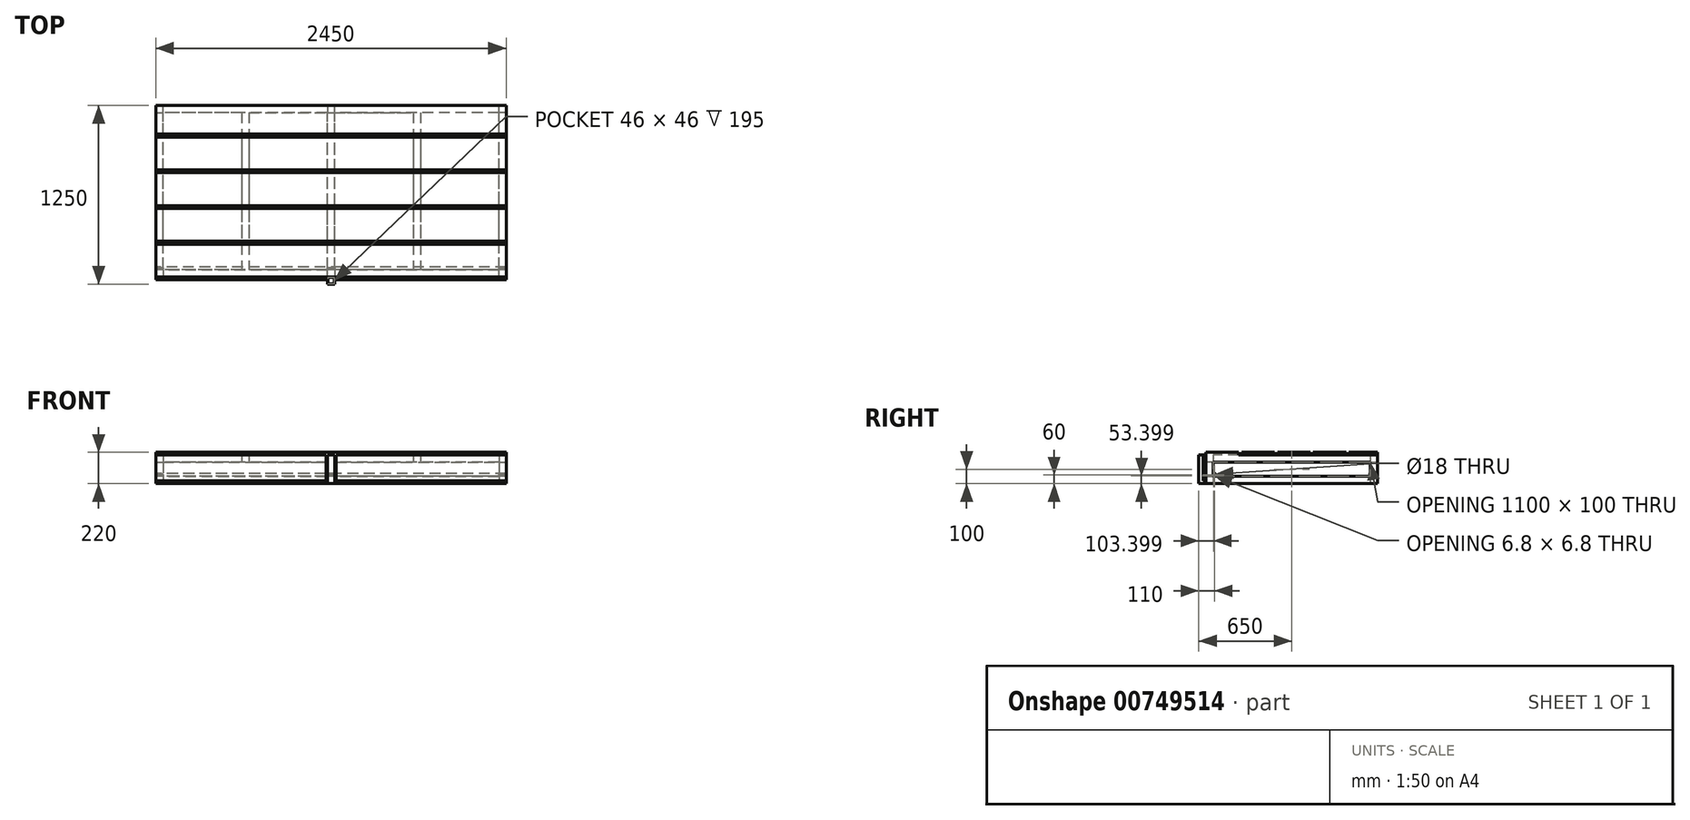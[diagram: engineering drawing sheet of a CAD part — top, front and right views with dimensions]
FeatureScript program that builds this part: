
annotation { "Feature Type Name" : "Feature", "Feature Type Description" : "" }
export const myFeature = defineFeature(function(context is Context, id is Id, definition is map)
    precondition{}
    {
        {
            var Q0;
            Q0=qCreatedBy(makeId("Top.planeOp"),FACE);
            var sketch = newSketch(context, id + "F0", { "sketchPlane" : qUnion([Q0])});
            skLineSegment(sketch, "E0.bottom", {"start": v(1225, -600) * mm, "end": v(-1225, -600) * mm});
            skLineSegment(sketch, "E0.top", {"start": v(1225, 600) * mm, "end": v(-1225, 600) * mm});
            skLineSegment(sketch, "E0.left", {"start": v(1225, -600) * mm, "end": v(1225, 600) * mm});
            skLineSegment(sketch, "E0.right", {"start": v(-1225, -600) * mm, "end": v(-1225, 600) * mm});
            skPoint(sketch, "E0.middle", {"position": v(0, 0) * mm});
            skLineSegment(sketch, "E1.0", {"start": v(1225, 550) * mm, "end": v(-1225, 550) * mm});
            skLineSegment(sketch, "E2.0", {"start": v(1227.5, -600) * mm, "end": v(1227.5, 600) * mm});
            skLineSegment(sketch, "E3.0", {"start": v(1175, -600) * mm, "end": v(1175, 600) * mm});
            skLineSegment(sketch, "E4.0", {"start": v(1225, -550) * mm, "end": v(-1225, -550) * mm});
            skLineSegment(sketch, "E5.0", {"start": v(-1175, -600) * mm, "end": v(-1175, 600) * mm});
            skLineSegment(sketch, "E6", {"start": v(0, 0) * mm, "end": v(0, 550) * mm});
            skLineSegment(sketch, "E7", {"start": v(0, 0) * mm, "end": v(0, -550) * mm});
            skLineSegment(sketch, "E8.0", {"start": v(25, 0) * mm, "end": v(25, 550) * mm});
            skLineSegment(sketch, "E9.0", {"start": v(-25, 0) * mm, "end": v(-25, 550) * mm});
            skLineSegment(sketch, "E10.0", {"start": v(-25, 0) * mm, "end": v(-25, -550) * mm});
            skLineSegment(sketch, "E11.0", {"start": v(25, 0) * mm, "end": v(25, -550) * mm});
            skSolve(sketch);
        }
        {
            var Q0;
            Q0=qSketchRegion(id+"F0",true);
            var Q1;
            {var subQ1=sQuery(id+"F0.wireOp",EDGE,"E6");Q1=makeQuery(id+"F0.imprint","IMPRINT",FACE,{"disambiguationData":[TD([[makeQuery(id+"F0.imprint","IMPRINT",EDGE,{"derivedFrom":subQ1}),-1.0]])]});}
            var Q2;
            {var subQ3=sQuery(id+"F0.wireOp",EDGE,"E6");Q2=makeQuery(id+"F0.imprint","IMPRINT",FACE,{"disambiguationData":[TD([[makeQuery(id+"F0.imprint","IMPRINT",EDGE,{"derivedFrom":subQ3}),1.0]])]});}
            extrude(context, id + "F1", {"entities" : qUnion([Q0, Q1, Q2]), "depth" : 50 * mm, "offsetDistance" : 25 * mm});
        }
        {
            var Q0;
            Q0=makeQuery(id+"F1.opExtrude","CAP_FACE",FACE,{"disambiguationData":[OSD([sQuery(id+"F0.wireOp",EDGE,"E0.bottom"),sQuery(id+"F0.wireOp",EDGE,"E0.top"),sQuery(id+"F0.wireOp",EDGE,"E0.left"),sQuery(id+"F0.wireOp",EDGE,"E0.right"),sQuery(id+"F0.wireOp",EDGE,"E1.0"),sQuery(id+"F0.wireOp",EDGE,"E3.0"),sQuery(id+"F0.wireOp",EDGE,"E4.0"),sQuery(id+"F0.wireOp",EDGE,"E5.0"),sQuery(id+"F0.wireOp",EDGE,"E8.0"),sQuery(id+"F0.wireOp",EDGE,"E9.0"),sQuery(id+"F0.wireOp",EDGE,"E10.0"),sQuery(id+"F0.wireOp",EDGE,"E11.0")])],"isStart":false});
            var sketch = newSketch(context, id + "F2", { "sketchPlane" : qUnion([Q0])});
            skLineSegment(sketch, "E12", {"start": v(-25, 550) * mm, "end": v(25, 550) * mm});
            skLineSegment(sketch, "E13", {"start": v(25, 550) * mm, "end": v(25, 600) * mm});
            skLineSegment(sketch, "E14", {"start": v(25, 600) * mm, "end": v(-25, 600) * mm});
            skLineSegment(sketch, "E15", {"start": v(-25, 600) * mm, "end": v(-25, 550) * mm});
            skLineSegment(sketch, "E16", {"start": v(-1175, 550) * mm, "end": v(-1175, 600) * mm});
            skLineSegment(sketch, "E17", {"start": v(-1175, 600) * mm, "end": v(-1225, 600) * mm});
            skLineSegment(sketch, "E18", {"start": v(-1225, 600) * mm, "end": v(-1225, 550) * mm});
            skLineSegment(sketch, "E19", {"start": v(-1225, 550) * mm, "end": v(-1175, 550) * mm});
            skLineSegment(sketch, "E20", {"start": v(-1175, -550) * mm, "end": v(-1175, -600) * mm});
            skLineSegment(sketch, "E21", {"start": v(-1175, -600) * mm, "end": v(-1225, -600) * mm});
            skLineSegment(sketch, "E22", {"start": v(-1225, -600) * mm, "end": v(-1225, -550) * mm});
            skLineSegment(sketch, "E23", {"start": v(-1225, -550) * mm, "end": v(-1175, -550) * mm});
            skLineSegment(sketch, "E24", {"start": v(-25, -550) * mm, "end": v(25, -550) * mm});
            skLineSegment(sketch, "E25", {"start": v(25, -550) * mm, "end": v(25, -600) * mm});
            skLineSegment(sketch, "E26", {"start": v(25, -600) * mm, "end": v(-25, -600) * mm});
            skPoint(sketch, "E26.endSnap0", {"position": v(0, -600) * mm});
            skLineSegment(sketch, "E27", {"start": v(-25, -600) * mm, "end": v(-25, -550) * mm});
            skLineSegment(sketch, "E28", {"start": v(1175, -550) * mm, "end": v(1225, -550) * mm});
            skLineSegment(sketch, "E29", {"start": v(1225, -550) * mm, "end": v(1225, -600) * mm});
            skLineSegment(sketch, "E30", {"start": v(1225, -600) * mm, "end": v(1175, -600) * mm});
            skLineSegment(sketch, "E31", {"start": v(1175, -600) * mm, "end": v(1175, -550) * mm});
            skLineSegment(sketch, "E32", {"start": v(1175, 550) * mm, "end": v(1175, 600) * mm});
            skLineSegment(sketch, "E33", {"start": v(1175, 600) * mm, "end": v(1225, 600) * mm});
            skLineSegment(sketch, "E34", {"start": v(1225, 600) * mm, "end": v(1225, 550) * mm});
            skLineSegment(sketch, "E35", {"start": v(1225, 550) * mm, "end": v(1175, 550) * mm});
            skSolve(sketch);
        }
        {
            var Q0;
            Q0=qSketchRegion(id+"F2",true);
            extrude(context, id + "F3", {"entities" : qUnion([Q0]), "operationType" : NewBodyOperationType.ADD, "depth" : 100 * mm, "offsetDistance" : 25 * mm});
        }
        {
            var Q0;
            Q0=makeQuery(id+"F3.opExtrude","CAP_FACE",FACE,{"disambiguationData":[OSD([sQuery(id+"F2.wireOp",EDGE,"E12"),sQuery(id+"F2.wireOp",EDGE,"E13"),sQuery(id+"F2.wireOp",EDGE,"E14"),sQuery(id+"F2.wireOp",EDGE,"E15")])],"isStart":false});
            var sketch = newSketch(context, id + "F4", { "sketchPlane" : qUnion([Q0])});
            skLineSegment(sketch, "E36.bottom", {"start": v(-1225, 600) * mm, "end": v(1225, 600) * mm});
            skLineSegment(sketch, "E36.top", {"start": v(-1225, -600) * mm, "end": v(1225, -600) * mm});
            skLineSegment(sketch, "E36.left", {"start": v(-1225, 600) * mm, "end": v(-1225, -600) * mm});
            skLineSegment(sketch, "E36.right", {"start": v(1225, 600) * mm, "end": v(1225, -600) * mm});
            skLineSegment(sketch, "E37.bottom", {"start": v(1175, -550) * mm, "end": v(-1175, -550) * mm});
            skLineSegment(sketch, "E37.top", {"start": v(1175, 550) * mm, "end": v(-1175, 550) * mm});
            skLineSegment(sketch, "E37.left", {"start": v(1175, -550) * mm, "end": v(1175, 550) * mm});
            skLineSegment(sketch, "E37.right", {"start": v(-1175, -550) * mm, "end": v(-1175, 550) * mm});
            skLineSegment(sketch, "E38.bottom", {"start": v(-25, 550) * mm, "end": v(25, 550) * mm});
            skLineSegment(sketch, "E38.top", {"start": v(-25, -550) * mm, "end": v(25, -550) * mm});
            skLineSegment(sketch, "E38.left", {"start": v(-25, 550) * mm, "end": v(-25, -550) * mm});
            skLineSegment(sketch, "E38.right", {"start": v(25, 550) * mm, "end": v(25, -550) * mm});
            skLineSegment(sketch, "E39", {"start": v(-25, 550) * mm, "end": v(-1175, 550) * mm});
            skLineSegment(sketch, "E40", {"start": v(-600, 550) * mm, "end": v(-600, -550) * mm});
            skLineSegment(sketch, "E41.0", {"start": v(-625, 550) * mm, "end": v(-625, -550) * mm});
            skLineSegment(sketch, "E42.0", {"start": v(-575, 550) * mm, "end": v(-575, -550) * mm});
            skLineSegment(sketch, "E43", {"start": v(25, 550) * mm, "end": v(1175, 550) * mm});
            skLineSegment(sketch, "E44", {"start": v(600, 550) * mm, "end": v(600, -550) * mm});
            skLineSegment(sketch, "E45.0", {"start": v(575, 550) * mm, "end": v(575, -550) * mm});
            skLineSegment(sketch, "E46.0", {"start": v(625, 550) * mm, "end": v(625, -550) * mm});
            skSolve(sketch);
        }
        {
            var Q0;
            Q0=qSketchRegion(id+"F4",true);
            var Q1;
            {var subQ0=sQuery(id+"F4.wireOp",EDGE,"E40");Q1=makeQuery(id+"F4.imprint","IMPRINT",FACE,{"disambiguationData":[TD([[makeQuery(id+"F4.imprint","IMPRINT",EDGE,{"derivedFrom":subQ0}),1.0]])]});}
            var Q2;
            {var subQ0=sQuery(id+"F4.wireOp",EDGE,"E40");Q2=makeQuery(id+"F4.imprint","IMPRINT",FACE,{"disambiguationData":[TD([[makeQuery(id+"F4.imprint","IMPRINT",EDGE,{"derivedFrom":subQ0}),-1.0]])]});}
            var Q3;
            {var subQ0=sQuery(id+"F4.wireOp",EDGE,"E44");Q3=makeQuery(id+"F4.imprint","IMPRINT",FACE,{"disambiguationData":[TD([[makeQuery(id+"F4.imprint","IMPRINT",EDGE,{"derivedFrom":subQ0}),1.0]])]});}
            var Q4;
            {var subQ0=sQuery(id+"F4.wireOp",EDGE,"E44");Q4=makeQuery(id+"F4.imprint","IMPRINT",FACE,{"disambiguationData":[TD([[makeQuery(id+"F4.imprint","IMPRINT",EDGE,{"derivedFrom":subQ0}),-1.0]])]});}
            var Q5;
            Q5=makeQuery(id+"F4.imprint","IMPRINT",FACE,{"disambiguationData":[TD([[makeQuery(id+"F4.imprint","IMPRINT",EDGE,{"derivedFrom":sQuery(id+"F4.wireOp",EDGE,"E38.bottom")}),-1.0]])]});
            extrude(context, id + "F5", {"entities" : qUnion([Q0, Q1, Q2, Q3, Q4, Q5]), "operationType" : NewBodyOperationType.ADD, "depth" : 50 * mm, "offsetDistance" : 25 * mm});
        }
        {
            var Q0;
            Q0=makeQuery(id+"F5.boolean.opBoolean","MERGE",FACE,{"derivedFrom":[makeQuery(id+"F3.boolean.opBoolean","MERGE",FACE,{"derivedFrom":[makeQuery(id+"F1.opExtrude","SWEPT_FACE",FACE,{"disambiguationData":[OSD([sQuery(id+"F0.wireOp",EDGE,"E0.right")])]}),makeQuery(id+"F3.opExtrude","SWEPT_FACE",FACE,{"disambiguationData":[OSD([sQuery(id+"F2.wireOp",EDGE,"E18")])]}),makeQuery(id+"F3.opExtrude","SWEPT_FACE",FACE,{"disambiguationData":[OSD([sQuery(id+"F2.wireOp",EDGE,"E22")])]})]}),makeQuery(id+"F5.opExtrude","SWEPT_FACE",FACE,{"disambiguationData":[OSD([sQuery(id+"F4.wireOp",EDGE,"E36.left")])]})]});
            var sketch = newSketch(context, id + "F6", { "sketchPlane" : qUnion([Q0])});
            skLineSegment(sketch, "E47", {"start": v(550, 50) * mm, "end": v(550, 60) * mm});
            skLineSegment(sketch, "E48", {"start": v(550, 60) * mm, "end": v(540, 60) * mm});
            skCircle(sketch, "E49", {"center": v(540, 60) * mm, "radius": 10.5 * mm});
            skCircle(sketch, "E50", {"center": v(540, 60) * mm, "radius": 9 * mm});
            skSolve(sketch);
        }
        {
            var Q0;
            Q0=qSketchRegion(id+"F6",true);
            extrude(context, id + "F7", {"entities" : qUnion([Q0]), "operationType" : NewBodyOperationType.ADD, "oppositeDirection" : true, "depth" : 2450 * mm, "offsetDistance" : 25 * mm});
        }
        {
            var Q0;
            Q0=makeQuery(id+"F5.boolean.opBoolean","MERGE",FACE,{"derivedFrom":[makeQuery(id+"F3.boolean.opBoolean","MERGE",FACE,{"derivedFrom":[makeQuery(id+"F1.opExtrude","SWEPT_FACE",FACE,{"disambiguationData":[OSD([sQuery(id+"F0.wireOp",EDGE,"E0.bottom")])]}),makeQuery(id+"F3.opExtrude","SWEPT_FACE",FACE,{"disambiguationData":[OSD([sQuery(id+"F2.wireOp",EDGE,"E21")])]}),makeQuery(id+"F3.opExtrude","SWEPT_FACE",FACE,{"disambiguationData":[OSD([sQuery(id+"F2.wireOp",EDGE,"E26")])]}),makeQuery(id+"F3.opExtrude","SWEPT_FACE",FACE,{"disambiguationData":[OSD([sQuery(id+"F2.wireOp",EDGE,"E30")])]})]}),makeQuery(id+"F5.opExtrude","SWEPT_FACE",FACE,{"disambiguationData":[OSD([sQuery(id+"F4.wireOp",EDGE,"E36.top")])]})]});
            var sketch = newSketch(context, id + "F8", { "sketchPlane" : qUnion([Q0])});
            skLineSegment(sketch, "E51.bottom", {"start": v(1225, 200) * mm, "end": v(-1275, 200) * mm});
            skLineSegment(sketch, "E51.top", {"start": v(1225, 20) * mm, "end": v(-1275, 20) * mm});
            skLineSegment(sketch, "E51.left", {"start": v(1225, 200) * mm, "end": v(1225, 20) * mm});
            skLineSegment(sketch, "E51.right", {"start": v(-1275, 200) * mm, "end": v(-1275, 20) * mm});
            skLineSegment(sketch, "E52", {"start": v(-1225, 200) * mm, "end": v(-1275, 200) * mm});
            skSolve(sketch);
        }
        {
            var Q0;
            Q0=qSketchRegion(id+"F8",true);
            extrude(context, id + "F9", {"entities" : qUnion([Q0]), "depth" : 20 * mm, "offsetDistance" : 25 * mm});
        }
        {
            var Q0;
            Q0=makeQuery(id+"F5.opExtrude","CAP_FACE",FACE,{"disambiguationData":[OSD([sQuery(id+"F4.wireOp",EDGE,"E36.bottom"),sQuery(id+"F4.wireOp",EDGE,"E36.top"),sQuery(id+"F4.wireOp",EDGE,"E36.left"),sQuery(id+"F4.wireOp",EDGE,"E36.right"),sQuery(id+"F4.wireOp",EDGE,"E37.bottom"),sQuery(id+"F4.wireOp",EDGE,"E37.left"),sQuery(id+"F4.wireOp",EDGE,"E37.right"),sQuery(id+"F4.wireOp",EDGE,"E38.left"),sQuery(id+"F4.wireOp",EDGE,"E38.right"),sQuery(id+"F4.wireOp",EDGE,"E39"),sQuery(id+"F4.wireOp",EDGE,"E41.0"),sQuery(id+"F4.wireOp",EDGE,"E42.0"),sQuery(id+"F4.wireOp",EDGE,"E43"),sQuery(id+"F4.wireOp",EDGE,"E45.0"),sQuery(id+"F4.wireOp",EDGE,"E46.0")])],"isStart":false});
            var sketch = newSketch(context, id + "F10", { "sketchPlane" : qUnion([Q0])});
            skLineSegment(sketch, "E53.bottom", {"start": v(1225, 600) * mm, "end": v(-1275, 600) * mm});
            skLineSegment(sketch, "E53.top", {"start": v(1225, -600) * mm, "end": v(-1275, -600) * mm});
            skLineSegment(sketch, "E53.left", {"start": v(1225, 600) * mm, "end": v(1225, -600) * mm});
            skLineSegment(sketch, "E53.right", {"start": v(-1275, 600) * mm, "end": v(-1275, -600) * mm});
            skSolve(sketch);
        }
        {
            var Q0;
            Q0=qSketchRegion(id+"F10",true);
            extrude(context, id + "F11", {"entities" : qUnion([Q0]), "depth" : 20 * mm, "offsetDistance" : 25 * mm});
        }
        {
            var Q0;
            Q0=makeQuery(id+"F9.opExtrude","SWEPT_FACE",FACE,{"disambiguationData":[OSD([sQuery(id+"F8.wireOp",EDGE,"E51.right")])]});
            extrude(context, id + "F12", {"entities" : qUnion([Q0]), "operationType" : NewBodyOperationType.REMOVE, "oppositeDirection" : true, "depth" : 110 * mm, "offsetDistance" : 25 * mm});
        }
        {
            var Q0;
            Q0=makeQuery(id+"F11.opExtrude","SWEPT_FACE",FACE,{"disambiguationData":[OSD([sQuery(id+"F10.wireOp",EDGE,"E53.right")])]});
            var sketch = newSketch(context, id + "F13", { "sketchPlane" : qUnion([Q0])});
            skLineSegment(sketch, "E54.bottom", {"start": v(600, 200) * mm, "end": v(620.46, 200) * mm});
            skLineSegment(sketch, "E54.top", {"start": v(600, 220) * mm, "end": v(620.46, 220) * mm});
            skLineSegment(sketch, "E54.left", {"start": v(600, 200) * mm, "end": v(600, 220) * mm});
            skLineSegment(sketch, "E54.right", {"start": v(620.46, 200) * mm, "end": v(620.46, 220) * mm});
            skLineSegment(sketch, "E55.1.0.0", {"start": v(350, 220) * mm, "end": v(370.46, 220) * mm});
            skLineSegment(sketch, "E55.1.0.1", {"start": v(370.46, 200) * mm, "end": v(370.46, 220) * mm});
            skLineSegment(sketch, "E55.1.0.2", {"start": v(350, 200) * mm, "end": v(370.46, 200) * mm});
            skLineSegment(sketch, "E55.1.0.3", {"start": v(350, 200) * mm, "end": v(350, 220) * mm});
            skLineSegment(sketch, "E55.2.0.0", {"start": v(100, 220) * mm, "end": v(120.46, 220) * mm});
            skLineSegment(sketch, "E55.2.0.1", {"start": v(120.46, 200) * mm, "end": v(120.46, 220) * mm});
            skLineSegment(sketch, "E55.2.0.2", {"start": v(100, 200) * mm, "end": v(120.46, 200) * mm});
            skLineSegment(sketch, "E55.2.0.3", {"start": v(100, 200) * mm, "end": v(100, 220) * mm});
            skLineSegment(sketch, "E55.3.0.0", {"start": v(-150, 220) * mm, "end": v(-129.54, 220) * mm});
            skLineSegment(sketch, "E55.3.0.1", {"start": v(-129.54, 200) * mm, "end": v(-129.54, 220) * mm});
            skLineSegment(sketch, "E55.3.0.2", {"start": v(-150, 200) * mm, "end": v(-129.54, 200) * mm});
            skLineSegment(sketch, "E55.3.0.3", {"start": v(-150, 200) * mm, "end": v(-150, 220) * mm});
            skLineSegment(sketch, "E55.4.0.0", {"start": v(-400, 220) * mm, "end": v(-379.54, 220) * mm});
            skLineSegment(sketch, "E55.4.0.1", {"start": v(-379.54, 200) * mm, "end": v(-379.54, 220) * mm});
            skLineSegment(sketch, "E55.4.0.2", {"start": v(-400, 200) * mm, "end": v(-379.54, 200) * mm});
            skLineSegment(sketch, "E55.4.0.3", {"start": v(-400, 200) * mm, "end": v(-400, 220) * mm});
            skLineSegment(sketch, "E55.direction1", {"start": v(600, 200) * mm, "end": v(350, 200) * mm, "construction": true});
            skSolve(sketch);
        }
        {
            var Q0;
            Q0=qSketchRegion(id+"F13",true);
            var Q1;
            Q1=makeQuery(id+"F11.opExtrude","SWEPT_FACE",FACE,{"disambiguationData":[OSD([sQuery(id+"F10.wireOp",EDGE,"E53.left")])]});
            extrude(context, id + "F14", {"entities" : qUnion([Q0]), "operationType" : NewBodyOperationType.REMOVE, "endBound" : BoundingType.UP_TO_SURFACE, "oppositeDirection" : true, "depth" : 25 * mm, "endBoundEntityFace" : qUnion([Q1]), "offsetDistance" : 25 * mm});
        }
        {
            var Q0;
            Q0=makeQuery(id+"F12.boolean.opBoolean","COPY",FACE,{"derivedFrom":makeQuery(id+"F12.opExtrude","CAP_FACE",FACE,{"disambiguationData":[OSD([sQuery(id+"F8.wireOp",EDGE,"E51.right")])],"isStart":false})});
            var Q1;
            Q1=makeQuery(id+"F5.boolean.opBoolean","MERGE",FACE,{"derivedFrom":[makeQuery(id+"F3.boolean.opBoolean","MERGE",FACE,{"derivedFrom":[makeQuery(id+"F1.opExtrude","SWEPT_FACE",FACE,{"disambiguationData":[OSD([sQuery(id+"F0.wireOp",EDGE,"E0.right")])]}),makeQuery(id+"F3.opExtrude","SWEPT_FACE",FACE,{"disambiguationData":[OSD([sQuery(id+"F2.wireOp",EDGE,"E18")])]}),makeQuery(id+"F3.opExtrude","SWEPT_FACE",FACE,{"disambiguationData":[OSD([sQuery(id+"F2.wireOp",EDGE,"E22")])]})]}),makeQuery(id+"F5.opExtrude","SWEPT_FACE",FACE,{"disambiguationData":[OSD([sQuery(id+"F4.wireOp",EDGE,"E36.left")])]})]});
            extrude(context, id + "F15", {"entities" : qUnion([Q0]), "endBound" : BoundingType.UP_TO_SURFACE, "depth" : 25 * mm, "endBoundEntityFace" : qUnion([Q1]), "offsetDistance" : 25 * mm});
        }
        {
            var Q0;
            Q0=makeQuery(id+"F9.opExtrude","SWEPT_BODY",BODY,{"disambiguationData":[OSD([sQuery(id+"F8.wireOp",EDGE,"E51.bottom"),sQuery(id+"F8.wireOp",EDGE,"E51.top"),sQuery(id+"F8.wireOp",EDGE,"E51.left"),sQuery(id+"F8.wireOp",EDGE,"E51.right"),sQuery(id+"F8.wireOp",EDGE,"E52")])]});
            var Q1;
            Q1=makeQuery(id+"F15.opExtrude","SWEPT_BODY",BODY,{"disambiguationData":[OSD([sQuery(id+"F8.wireOp",EDGE,"E51.right")])]});
            booleanBodies(context, id + "F16", {"operationType" : BooleanOperationType.UNION, "tools" : qUnion([Q0, Q1])});
        }
        {
            var Q0;
            Q0=makeQuery(id+"F11.opExtrude","SWEPT_FACE",FACE,{"disambiguationData":[OSD([sQuery(id+"F10.wireOp",EDGE,"E53.top")])]});
            var sketch = newSketch(context, id + "F17", { "sketchPlane" : qUnion([Q0])});
            skLineSegment(sketch, "E56.bottom", {"start": v(-1225, 200) * mm, "end": v(-1275, 200) * mm});
            skLineSegment(sketch, "E56.top", {"start": v(-1225, 220) * mm, "end": v(-1275, 220) * mm});
            skLineSegment(sketch, "E56.left", {"start": v(-1225, 200) * mm, "end": v(-1225, 220) * mm});
            skLineSegment(sketch, "E56.right", {"start": v(-1275, 200) * mm, "end": v(-1275, 220) * mm});
            skSolve(sketch);
        }
        {
            var Q0;
            Q0=qSketchRegion(id+"F17",true);
            extrude(context, id + "F18", {"entities" : qUnion([Q0]), "operationType" : NewBodyOperationType.REMOVE, "endBound" : BoundingType.THROUGH_ALL, "oppositeDirection" : true, "depth" : 25 * mm, "offsetDistance" : 25 * mm});
        }
        {
            var Q0;
            Q0=makeQuery(id+"F1.opExtrude","CAP_FACE",FACE,{"disambiguationData":[OSD([sQuery(id+"F0.wireOp",EDGE,"E0.bottom"),sQuery(id+"F0.wireOp",EDGE,"E0.top"),sQuery(id+"F0.wireOp",EDGE,"E0.left"),sQuery(id+"F0.wireOp",EDGE,"E0.right"),sQuery(id+"F0.wireOp",EDGE,"E1.0"),sQuery(id+"F0.wireOp",EDGE,"E3.0"),sQuery(id+"F0.wireOp",EDGE,"E4.0"),sQuery(id+"F0.wireOp",EDGE,"E5.0"),sQuery(id+"F0.wireOp",EDGE,"E8.0"),sQuery(id+"F0.wireOp",EDGE,"E9.0"),sQuery(id+"F0.wireOp",EDGE,"E10.0"),sQuery(id+"F0.wireOp",EDGE,"E11.0")])],"isStart":true});
            var sketch = newSketch(context, id + "F19", { "sketchPlane" : qUnion([Q0])});
            skLineSegment(sketch, "E57.top", {"start": v(-25, 600) * mm, "end": v(25, 600) * mm});
            skLineSegment(sketch, "E58.top", {"start": v(-25, 650) * mm, "end": v(25, 650) * mm});
            skLineSegment(sketch, "E58.left", {"start": v(-25, 600) * mm, "end": v(-25, 650) * mm});
            skLineSegment(sketch, "E58.right", {"start": v(25, 600) * mm, "end": v(25, 650) * mm});
            skLineSegment(sketch, "E59", {"start": v(-25, 650) * mm, "end": v(-35, 650) * mm});
            skLineSegment(sketch, "E60", {"start": v(-35, 650) * mm, "end": v(-35, 600) * mm});
            skLineSegment(sketch, "E61", {"start": v(-35, 600) * mm, "end": v(-25, 600) * mm});
            skLineSegment(sketch, "E62", {"start": v(25, 650) * mm, "end": v(35, 650) * mm});
            skLineSegment(sketch, "E63", {"start": v(35, 650) * mm, "end": v(35, 600) * mm});
            skLineSegment(sketch, "E64", {"start": v(35, 600) * mm, "end": v(25, 600) * mm});
            skSolve(sketch);
        }
        {
            var Q0;
            Q0=qSketchRegion(id+"F19",true);
            var Q1;
            {var subQ0=sQuery(id+"F8.wireOp",EDGE,"E52");Q1=makeQuery(id+"F16.opBoolean","MERGE",FACE,{"derivedFrom":[makeQuery(id+"F9.opExtrude","SWEPT_FACE",FACE,{"disambiguationData":[OSD([sQuery(id+"F8.wireOp",EDGE,"E51.bottom"),subQ0])]}),makeQuery(id+"F15.opExtrude","SWEPT_FACE",FACE,{"disambiguationData":[OSD([sQuery(id+"F8.wireOp",EDGE,"E51.right"),subQ0])]})]});}
            extrude(context, id + "F20", {"entities" : qUnion([Q0]), "operationType" : NewBodyOperationType.REMOVE, "endBound" : BoundingType.UP_TO_SURFACE, "oppositeDirection" : true, "depth" : 25 * mm, "endBoundEntityFace" : qUnion([Q1]), "offsetDistance" : 25 * mm});
        }
        {
            var Q0;
            Q0=makeQuery(id+"F1.opExtrude","CAP_FACE",FACE,{"disambiguationData":[OSD([sQuery(id+"F0.wireOp",EDGE,"E0.bottom"),sQuery(id+"F0.wireOp",EDGE,"E0.top"),sQuery(id+"F0.wireOp",EDGE,"E0.left"),sQuery(id+"F0.wireOp",EDGE,"E0.right"),sQuery(id+"F0.wireOp",EDGE,"E1.0"),sQuery(id+"F0.wireOp",EDGE,"E3.0"),sQuery(id+"F0.wireOp",EDGE,"E4.0"),sQuery(id+"F0.wireOp",EDGE,"E5.0"),sQuery(id+"F0.wireOp",EDGE,"E8.0"),sQuery(id+"F0.wireOp",EDGE,"E9.0"),sQuery(id+"F0.wireOp",EDGE,"E10.0"),sQuery(id+"F0.wireOp",EDGE,"E11.0")])],"isStart":true});
            var sketch = newSketch(context, id + "F21", { "sketchPlane" : qUnion([Q0])});
            skLineSegment(sketch, "E65", {"start": v(-25, 550) * mm, "end": v(-25, 600) * mm});
            skLineSegment(sketch, "E66", {"start": v(-25, 600) * mm, "end": v(-25, 650) * mm});
            skLineSegment(sketch, "E67", {"start": v(-25, 650) * mm, "end": v(25, 650) * mm});
            skLineSegment(sketch, "E68", {"start": v(25, 650) * mm, "end": v(25, 600) * mm});
            skLineSegment(sketch, "E69", {"start": v(25, 600) * mm, "end": v(-25, 600) * mm});
            skSolve(sketch);
        }
        {
            var Q0;
            Q0=qSketchRegion(id+"F21",true);
            extrude(context, id + "F22", {"entities" : qUnion([Q0]), "operationType" : NewBodyOperationType.ADD, "oppositeDirection" : true, "depth" : 5 * mm, "offsetDistance" : 25 * mm});
        }
        {
            var Q0;
            Q0=makeQuery(id+"F22.opExtrude","CAP_FACE",FACE,{"disambiguationData":[OSD([sQuery(id+"F21.wireOp",EDGE,"E66"),sQuery(id+"F21.wireOp",EDGE,"E67"),sQuery(id+"F21.wireOp",EDGE,"E68"),sQuery(id+"F21.wireOp",EDGE,"E69")])],"isStart":false});
            var sketch = newSketch(context, id + "F23", { "sketchPlane" : qUnion([Q0])});
            skLineSegment(sketch, "E70.bottom", {"start": v(-25, -600) * mm, "end": v(25, -600) * mm});
            skLineSegment(sketch, "E70.top", {"start": v(-25, -650) * mm, "end": v(25, -650) * mm});
            skLineSegment(sketch, "E70.left", {"start": v(-25, -600) * mm, "end": v(-25, -650) * mm});
            skLineSegment(sketch, "E70.right", {"start": v(25, -600) * mm, "end": v(25, -650) * mm});
            skLineSegment(sketch, "E71.bottom", {"start": v(25, -650) * mm, "end": v(23, -650) * mm});
            skLineSegment(sketch, "E71.top", {"start": v(25, -648) * mm, "end": v(23, -648) * mm});
            skLineSegment(sketch, "E71.left", {"start": v(25, -650) * mm, "end": v(25, -648) * mm});
            skLineSegment(sketch, "E71.right", {"start": v(23, -650) * mm, "end": v(23, -648) * mm});
            skLineSegment(sketch, "E72.bottom", {"start": v(23, -648) * mm, "end": v(-23, -648) * mm});
            skLineSegment(sketch, "E72.top", {"start": v(23, -602) * mm, "end": v(-23, -602) * mm});
            skLineSegment(sketch, "E72.left", {"start": v(23, -648) * mm, "end": v(23, -602) * mm});
            skLineSegment(sketch, "E72.right", {"start": v(-23, -648) * mm, "end": v(-23, -602) * mm});
            skSolve(sketch);
        }
        {
            var Q0;
            Q0=qSketchRegion(id+"F23",true);
            var Q1;
            {var subQ0=sQuery(id+"F8.wireOp",EDGE,"E51.right");var subQ1=sQuery(id+"F8.wireOp",EDGE,"E51.left");var subQ2=sQuery(id+"F8.wireOp",EDGE,"E52");var subQ4=sQuery(id+"F8.wireOp",EDGE,"E51.bottom");Q1=makeQuery(id+"F20.boolean.opBoolean","SPLIT",FACE,{"disambiguationData":[TD([makeQuery(id+"F9.opExtrude","SWEPT_FACE",FACE,{"disambiguationData":[OSD([subQ1])]})])],"derivedFrom":makeQuery(id+"F16.opBoolean","MERGE",FACE,{"derivedFrom":[makeQuery(id+"F9.opExtrude","SWEPT_FACE",FACE,{"disambiguationData":[OSD([subQ4,subQ2])]}),makeQuery(id+"F15.opExtrude","SWEPT_FACE",FACE,{"disambiguationData":[OSD([subQ0,subQ2])]})]})});}
            extrude(context, id + "F24", {"entities" : qUnion([Q0]), "operationType" : NewBodyOperationType.ADD, "endBound" : BoundingType.UP_TO_SURFACE, "depth" : 25 * mm, "endBoundEntityFace" : qUnion([Q1]), "offsetDistance" : 25 * mm});
        }
    });
